# Revit family: Letter_Boxes-Salsbury_Industries-Surface_Mounted_Mailboxes
name_source: partatom
category: Specialty Equipment
revit_build: Autodesk Revit 2016 (Build: 20150714_1515(x64)
units: mm (PartAtom-declared; Revit-internal decimal feet)

## family parameters
Always vertical = Yes
Cut with Voids When Loaded = No
OmniClass Number = 23.40.90.14.11
OmniClass Title = Mail Boxes
Part Type = Normal
Room Calculation Point = No
Round Connector Dimension = Use Diameter
Shared = No
Work Plane-Based = No

## types (3) — shared parameters
Assembly Code = C1030910
Assembly Description = Mailboxes
Back Enclosure Material = Aluminum - Salsbury Finish - Clear
Front Panel Material = Paint - Salsbury Finish - Sandstone
Height = 18.937 "
Horizontal Lock Offset = 2.438 "
Lock Material = Stainless Steel - Salsbury Finish -  Polished
Manufacturer = Salsbury Industries
MasterFormat Number = 10 55 00
MasterFormat Title = Postal Specialties
OmniClass 23 Number = 23.40.90.14.11
OmniClass 23 Title = Mail Boxes
URL = www.mailboxes.com
Version = 1.0 (05/31/19)
Vertical Lock Offset = 7.988 "

## per-type parameters (varying)
| type | Depth | Description | Internal Enclosure Depth | Model | Private Access Commercial Lock | Type Comments | Width |
| 2240 - USPS Access | 7.5 " | USPS Access - Surface Mounted | 6.75 " | 2240 | No | Letter Box - Standard | 15 " |
| 2240 - Private Access | 7.5 " | Private Access - Surface Mounted | 6.75 " | 2240 | Yes | Letter Box - Standard | 15 " |
| 2260 - Private Access | 3.75 " | Private Access - Surface Mounted | 3.5 " | 2260 | Yes | Letter Box - Slim | 11 " |

## geometry (parser evidence)
native form markers: Sweep x2
no freeform markers — native parametric forms only
